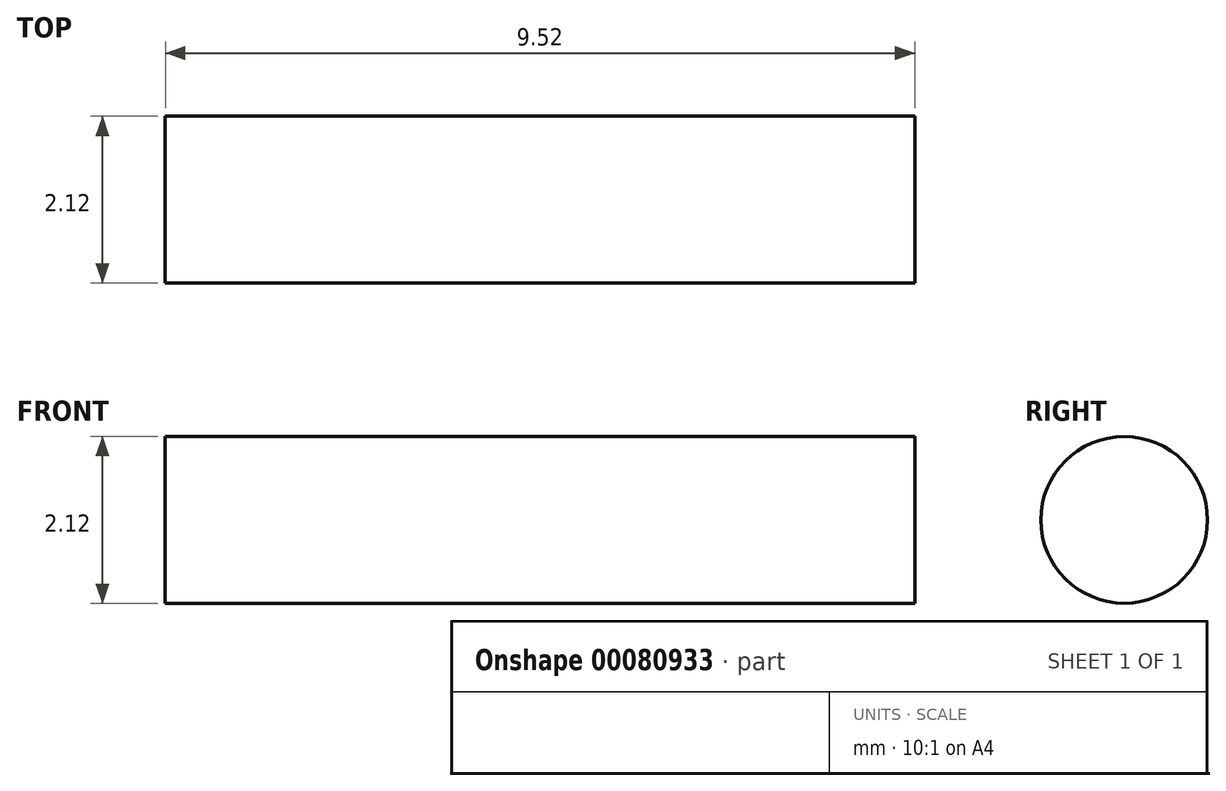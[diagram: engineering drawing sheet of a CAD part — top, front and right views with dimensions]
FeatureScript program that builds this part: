
annotation { "Feature Type Name" : "Feature", "Feature Type Description" : "" }
export const myFeature = defineFeature(function(context is Context, id is Id, definition is map)
    precondition{}
    {
        {
            var Q0;
            Q0=qCreatedBy(makeId("Right.planeOp"),FACE);
            var sketch = newSketch(context, id + "F0", { "sketchPlane" : qUnion([Q0])});
            skCircle(sketch, "E0", {"center": v(0, 0) * mm, "radius": 1.06 * mm});
            skSolve(sketch);
        }
        {
            var Q0;
            Q0=makeQuery(id+"F0.imprint","IMPRINT",FACE,{"disambiguationData":[TD([[makeQuery(id+"F0.imprint","IMPRINT",EDGE,{"derivedFrom":sQuery(id+"F0.wireOp",EDGE,"E0")}),1.0]])]});
            extrude(context, id + "F1", {"entities" : qUnion([Q0]), "depth" : 9.52 * mm, "symmetric" : true});
        }
    });
